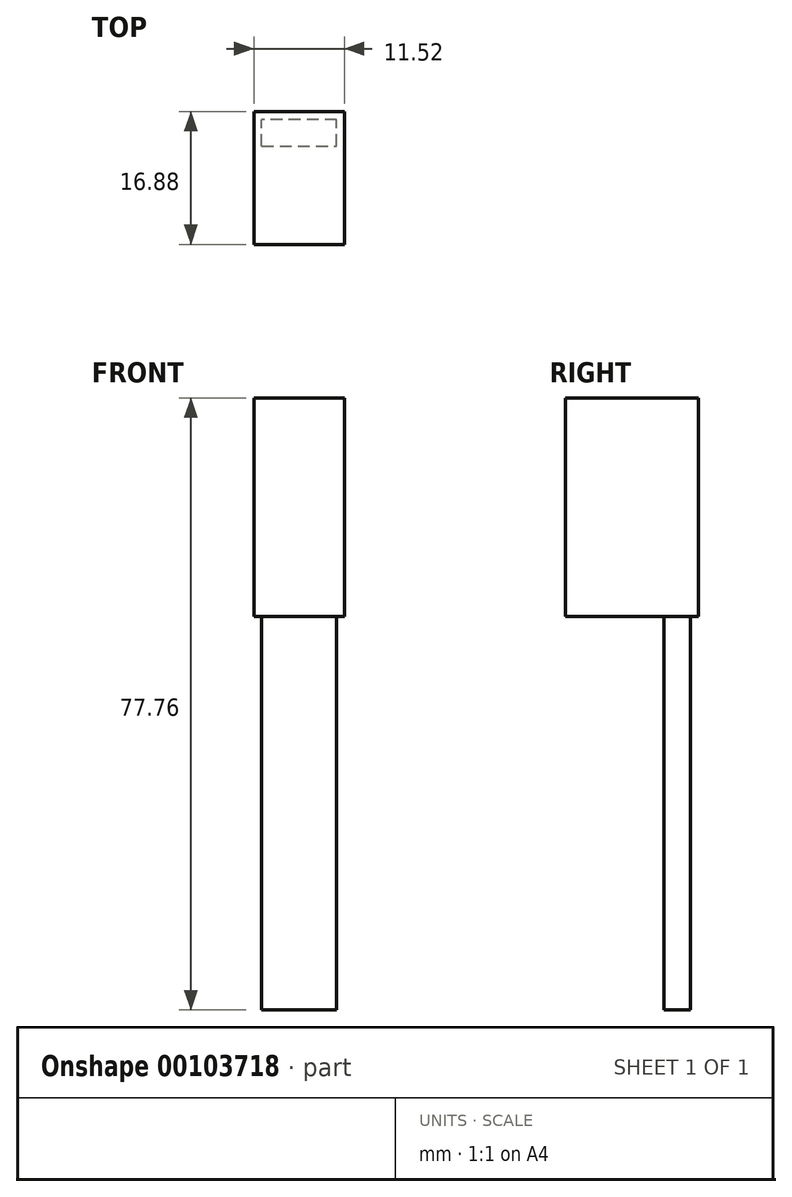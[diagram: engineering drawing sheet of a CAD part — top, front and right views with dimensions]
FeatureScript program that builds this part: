
annotation { "Feature Type Name" : "Feature", "Feature Type Description" : "" }
export const myFeature = defineFeature(function(context is Context, id is Id, definition is map)
    precondition{}
    {
        {
            var Q0;
            Q0=qCreatedBy(makeId("Front.planeOp"),FACE);
            var sketch = newSketch(context, id + "F0", { "sketchPlane" : qUnion([Q0])});
            skLineSegment(sketch, "E0.bottom", {"start": v(-4.76, 38.88) * mm, "end": v(4.76, 38.88) * mm});
            skLineSegment(sketch, "E0.top", {"start": v(-4.76, -38.88) * mm, "end": v(4.76, -38.88) * mm});
            skLineSegment(sketch, "E0.left", {"start": v(-4.76, 38.88) * mm, "end": v(-4.76, -38.88) * mm});
            skLineSegment(sketch, "E0.right", {"start": v(4.76, 38.88) * mm, "end": v(4.76, -38.88) * mm});
            skPoint(sketch, "E0.middle", {"position": v(0, 0) * mm});
            skSolve(sketch);
        }
        {
            var Q0;
            Q0=makeQuery(id+"F0.imprint","IMPRINT",FACE,{"disambiguationData":[TD([[makeQuery(id+"F0.imprint","IMPRINT",EDGE,{"derivedFrom":sQuery(id+"F0.wireOp",EDGE,"E0.bottom")}),-1.0]])]});
            extrude(context, id + "F1", {"entities" : qUnion([Q0]), "depth" : 15.88 * mm});
        }
        {
            var Q0;
            Q0=makeQuery(id+"F1.opExtrude","SWEPT_FACE",FACE,{"disambiguationData":[OSD([sQuery(id+"F0.wireOp",EDGE,"E0.right")])]});
            var sketch = newSketch(context, id + "F2", { "sketchPlane" : qUnion([Q0])});
            skLineSegment(sketch, "E1.bottom", {"start": v(-15.88, -38.88) * mm, "end": v(-3.39, -38.88) * mm});
            skLineSegment(sketch, "E1.top", {"start": v(-15.88, 11.12) * mm, "end": v(-3.39, 11.12) * mm});
            skLineSegment(sketch, "E1.left", {"start": v(-15.88, -38.88) * mm, "end": v(-15.88, 11.12) * mm});
            skLineSegment(sketch, "E1.right", {"start": v(-3.39, -38.88) * mm, "end": v(-3.39, 11.12) * mm});
            skSolve(sketch);
        }
        {
            var Q0;
            Q0=makeQuery(id+"F2.imprint","IMPRINT",FACE,{"disambiguationData":[TD([[makeQuery(id+"F2.imprint","IMPRINT",EDGE,{"derivedFrom":sQuery(id+"F2.wireOp",EDGE,"E1.bottom")}),1.0]])]});
            extrude(context, id + "F3", {"entities" : qUnion([Q0]), "operationType" : NewBodyOperationType.REMOVE, "oppositeDirection" : true, "depth" : 25 * mm});
        }
        {
            var Q0;
            Q0=makeQuery(id+"F1.opExtrude","SWEPT_FACE",FACE,{"disambiguationData":[OSD([sQuery(id+"F0.wireOp",EDGE,"E0.left")])]});
            var sketch = newSketch(context, id + "F4", { "sketchPlane" : qUnion([Q0])});
            skLineSegment(sketch, "E2", {"start": v(3.39, 11.12) * mm, "end": v(0, 11.12) * mm});
            skSolve(sketch);
        }
        {
            var Q0;
            {var subQ3=sQuery(id+"F4.wireOp",EDGE,"E2");Q0=makeQuery(id+"F4.imprint","IMPRINT",FACE,{"disambiguationData":[TD([[makeQuery(id+"F4.imprint","IMPRINT",EDGE,{"derivedFrom":subQ3}),-1.0]])]});}
            extrude(context, id + "F5", {"entities" : qUnion([Q0]), "operationType" : NewBodyOperationType.ADD, "depth" : 1 * mm});
        }
        {
            var Q0;
            Q0=makeQuery(id+"F1.opExtrude","SWEPT_FACE",FACE,{"disambiguationData":[OSD([sQuery(id+"F0.wireOp",EDGE,"E0.right")])]});
            var sketch = newSketch(context, id + "F6", { "sketchPlane" : qUnion([Q0])});
            skLineSegment(sketch, "E3", {"start": v(-3.39, 11.12) * mm, "end": v(0, 11.12) * mm});
            skSolve(sketch);
        }
        {
            var Q0;
            {var subQ1=sQuery(id+"F6.wireOp",EDGE,"E3");Q0=makeQuery(id+"F6.imprint","IMPRINT",FACE,{"disambiguationData":[TD([[makeQuery(id+"F6.imprint","IMPRINT",EDGE,{"derivedFrom":subQ1}),1.0]])]});}
            extrude(context, id + "F7", {"entities" : qUnion([Q0]), "operationType" : NewBodyOperationType.ADD, "depth" : 1 * mm});
        }
        {
            var Q0;
            {var subQ0=sQuery(id+"F0.wireOp",EDGE,"E0.right");var subQ1=makeQuery(id+"F1.opExtrude","CAP_EDGE",EDGE,{"disambiguationData":[OSD([subQ0])],"isStart":true});var subQ2=sQuery(id+"F0.wireOp",EDGE,"E0.bottom");var subQ3=sQuery(id+"F0.wireOp",EDGE,"E0.left");var subQ4=makeQuery(id+"F1.opExtrude","CAP_EDGE",EDGE,{"disambiguationData":[OSD([subQ3])],"isStart":true});Q0=makeQuery(id+"F7.boolean.opBoolean","MERGE",FACE,{"derivedFrom":[makeQuery(id+"F5.boolean.opBoolean","MERGE",FACE,{"derivedFrom":[makeQuery(id+"F1.opExtrude","CAP_FACE",FACE,{"disambiguationData":[OSD([subQ2,sQuery(id+"F0.wireOp",EDGE,"E0.top"),subQ3,subQ0])],"isStart":true}),makeQuery(id+"F5.opExtrude","SWEPT_FACE",FACE,{"disambiguationData":[OSD([subQ3]),TDD([makeQuery(id+"F4.imprint","IMPRINT",EDGE,{"disambiguationData":[TD([[makeQuery(id+"F4.imprint","INTERSECT",VERTEX,{"derivedFrom":[subQ4,sQuery(id+"F4.wireOp",EDGE,"E2")]}),1.0]])],"derivedFrom":subQ4})])]})]}),makeQuery(id+"F7.opExtrude","SWEPT_FACE",FACE,{"disambiguationData":[OSD([subQ0]),TDD([makeQuery(id+"F6.imprint","IMPRINT",EDGE,{"disambiguationData":[TD([[makeQuery(id+"F6.imprint","INTERSECT",VERTEX,{"derivedFrom":[subQ1,sQuery(id+"F6.wireOp",EDGE,"E3")]}),1.0]])],"derivedFrom":subQ1})])]})]});}
            var sketch = newSketch(context, id + "F8", { "sketchPlane" : qUnion([Q0])});
            skLineSegment(sketch, "E4", {"start": v(-5.76, 11.12) * mm, "end": v(5.76, 11.12) * mm});
            skSolve(sketch);
        }
        {
            var Q0;
            {var subQ0=sQuery(id+"F0.wireOp",EDGE,"E0.left");var subQ1=makeQuery(id+"F1.opExtrude","CAP_EDGE",EDGE,{"disambiguationData":[OSD([subQ0])],"isStart":true});var subQ4=makeQuery(id+"F5.opExtrude","CAP_EDGE",EDGE,{"disambiguationData":[OSD([subQ0]),TDD([makeQuery(id+"F4.imprint","IMPRINT",EDGE,{"disambiguationData":[TD([[makeQuery(id+"F4.imprint","INTERSECT",VERTEX,{"derivedFrom":[subQ1,sQuery(id+"F4.wireOp",EDGE,"E2")]}),1.0]])],"derivedFrom":subQ1})])],"isStart":false});Q0=makeQuery(id+"F8.imprint","IMPRINT",FACE,{"disambiguationData":[TD([[makeQuery(id+"F8.imprint","IMPRINT",EDGE,{"derivedFrom":subQ4}),-1.0]])]});}
            extrude(context, id + "F9", {"entities" : qUnion([Q0]), "operationType" : NewBodyOperationType.ADD, "depth" : 1 * mm});
        }
    });
